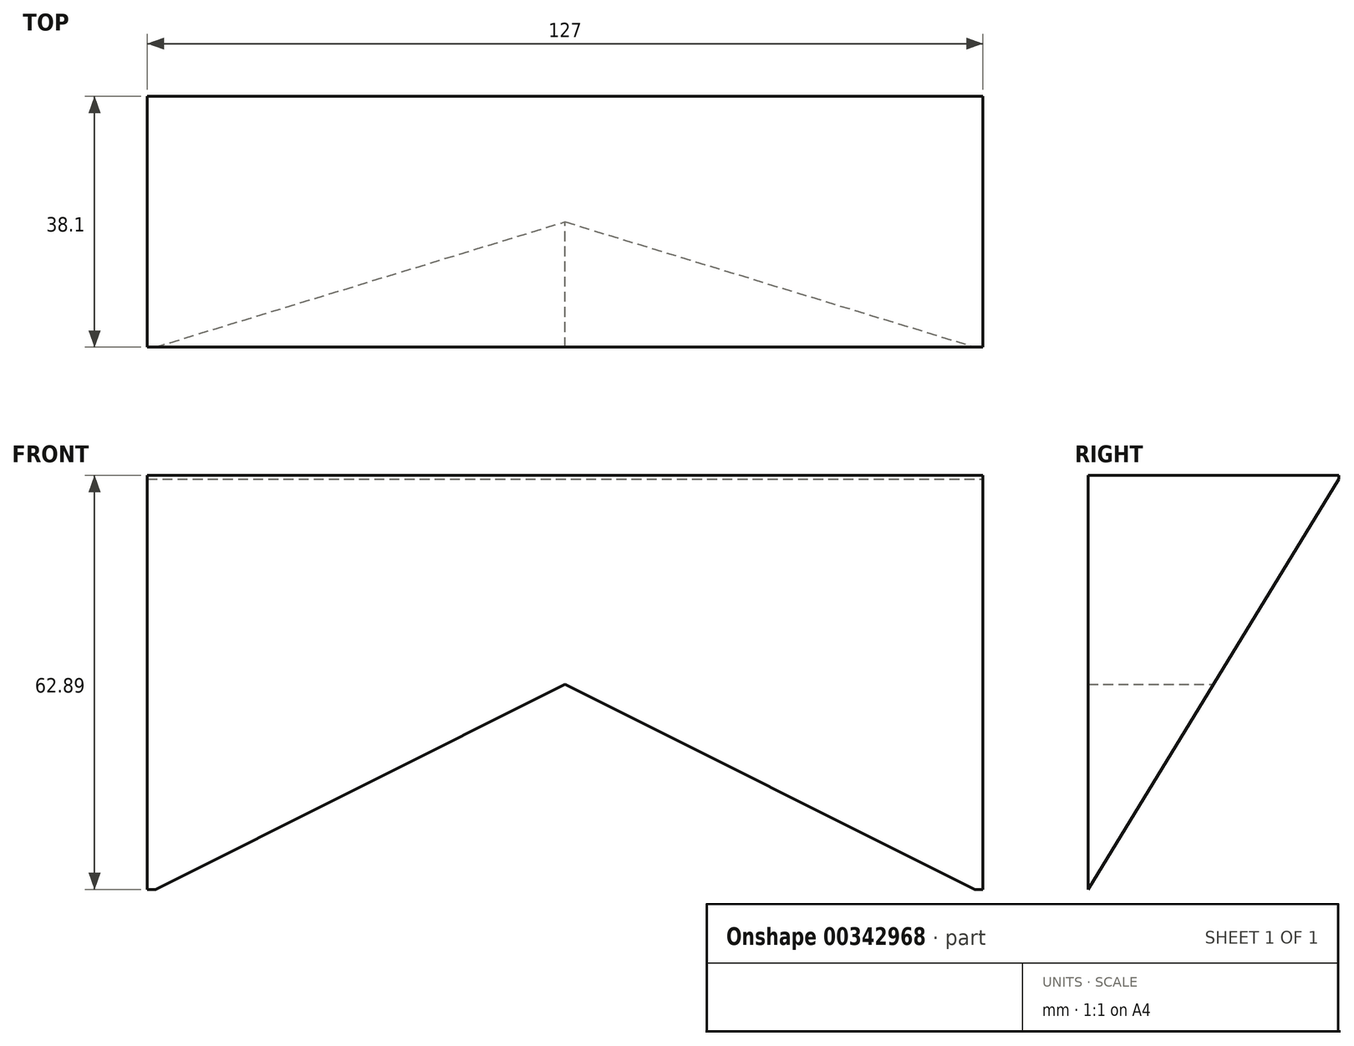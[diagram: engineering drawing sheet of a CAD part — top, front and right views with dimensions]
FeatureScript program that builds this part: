
annotation { "Feature Type Name" : "Feature", "Feature Type Description" : "" }
export const myFeature = defineFeature(function(context is Context, id is Id, definition is map)
    precondition{}
    {
        {
            var Q0;
            Q0=qCreatedBy(makeId("Front.planeOp"),FACE);
            var sketch = newSketch(context, id + "F0", { "sketchPlane" : qUnion([Q0])});
            skLineSegment(sketch, "E0", {"start": v(-64.96, 27.21) * mm, "end": v(62.04, 27.21) * mm});
            skLineSegment(sketch, "E1", {"start": v(-64.96, 27.21) * mm, "end": v(-64.96, -36.29) * mm});
            skLineSegment(sketch, "E2", {"start": v(62.04, 27.21) * mm, "end": v(62.04, -36.29) * mm});
            skLineSegment(sketch, "E3", {"start": v(-1.46, 27.21) * mm, "end": v(-1.46, -4.54) * mm});
            skLineSegment(sketch, "E4", {"start": v(-64.96, -36.29) * mm, "end": v(-1.46, -4.54) * mm});
            skLineSegment(sketch, "E5", {"start": v(-1.46, -4.54) * mm, "end": v(62.04, -36.29) * mm});
            skSolve(sketch);
        }
        {
            var Q0;
            Q0 = qSketchRegion(id + "F0", true);
            extrude(context, id + "F1", {"entities" : qUnion([Q0]), "depth" : 38.1 * mm});
        }
        {
            var Q0;
            Q0=qCreatedBy(makeId("Right.planeOp"),FACE);
            var sketch = newSketch(context, id + "F2", { "sketchPlane" : qUnion([Q0])});
            skLineSegment(sketch, "E6", {"start": v(-38.47, -36.29) * mm, "end": v(0, -36.29) * mm});
            skLineSegment(sketch, "E7", {"start": v(0, -36.29) * mm, "end": v(0, 26.67) * mm});
            skLineSegment(sketch, "E8", {"start": v(0, 26.67) * mm, "end": v(-38.47, -36.29) * mm});
            skSolve(sketch);
        }
        {
            var Q0;
            Q0 = qSketchRegion(id + "F2", true);
            extrude(context, id + "F3", {"entities" : qUnion([Q0]), "operationType" : NewBodyOperationType.REMOVE, "oppositeDirection" : true, "depth" : 98.55 * mm, "hasSecondDirection" : true, "secondDirectionOppositeDirection" : false, "secondDirectionDepth" : 78.23 * mm});
        }
    });
